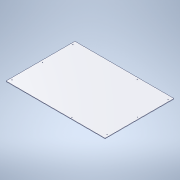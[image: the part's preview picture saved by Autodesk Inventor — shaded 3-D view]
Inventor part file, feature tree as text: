
AUTODESK INVENTOR PART (.ipt)
format: ipt  version: 2020 (Build 240168000, 168)  size: 125,952 bytes
history: native  units: mm
features: sketch x3, hole x2, extrude x1
ambient origin geometry x8: Origin, YZ Plane, XZ Plane, XY Plane, X Axis, Y Axis, Z Axis, Center Point
bodies: Solid1 (feature_tree)
feature tree (6):
  extrude  "Extrusion1"  Depth=1000.0mm
  hole  "Hole1"  [1 undecoded]
  hole  "Hole2"  [1 undecoded]
  sketch  "Sketch1"  dims[d0=695.0mm d1=1000.0mm]
  sketch  "Sketch2"  dims[d2=5.0mm d3=0.0mm d4=40.0mm]
  sketch  "Sketch3"  dims[d5=20.0mm d6=20.0mm d7=20.0mm d8=347.5mm d9=40.0mm d14=40.0mm d15=40.0mm d16=347.5mm d17=20.0mm d18=20.0mm d19=20.0mm d20=5.5mm d21=6.0mm d22=11.5mm d23=2.0mm d24=90.0deg d25=5.0mm d26=0.0mm d27=350.0mm d28=15.0mm d29=20.0mm d30=350.0mm d31=5.5mm d32=16.0mm d33=10.0mm d34=2.0mm d35=90.0deg d36=8.0mm d37=20.594885mm]
note: 2 required parameter values undecoded (feature->parameter linkage not recoverable at this tier; creation-order binding heuristic only, values carry confidence <= 0.55)
